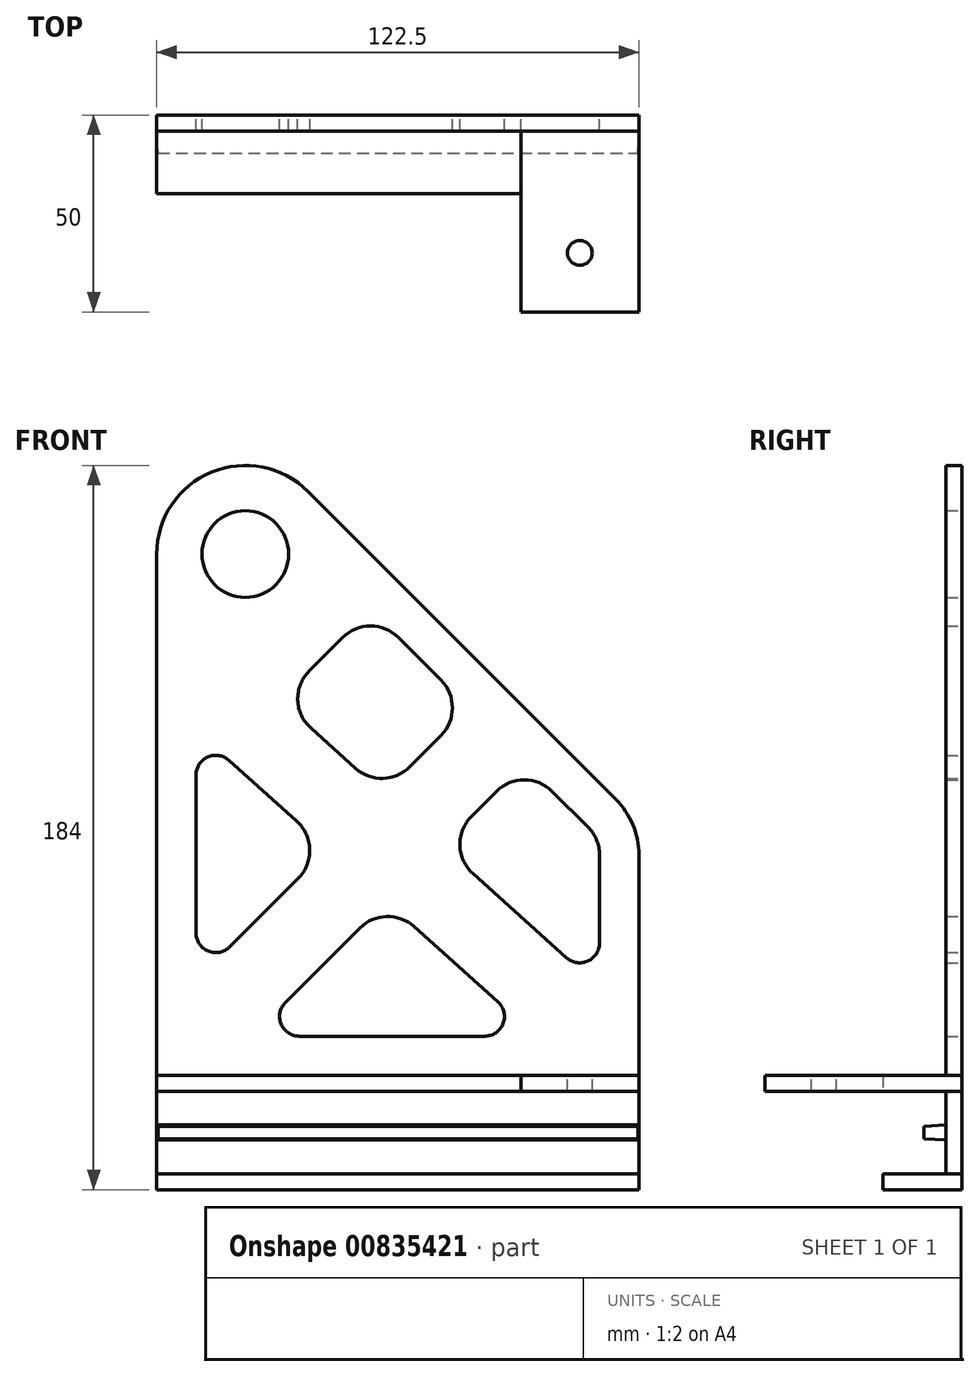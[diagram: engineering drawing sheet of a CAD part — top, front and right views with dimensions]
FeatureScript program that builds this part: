
annotation { "Feature Type Name" : "Feature", "Feature Type Description" : "" }
export const myFeature = defineFeature(function(context is Context, id is Id, definition is map)
    precondition{}
    {
        {
            var Q0;
            Q0=qCreatedBy(makeId("Front.planeOp"),FACE);
            var sketch = newSketch(context, id + "F0", { "sketchPlane" : qUnion([Q0])});
            skLineSegment(sketch, "E0.bottom", {"start": v(0, 0) * mm, "end": v(122.5, 0) * mm});
            skLineSegment(sketch, "E0.top", {"start": v(0, -4) * mm, "end": v(122.5, -4) * mm});
            skLineSegment(sketch, "E0.left", {"start": v(0, 0) * mm, "end": v(0, -4) * mm});
            skLineSegment(sketch, "E0.right", {"start": v(122.5, 0) * mm, "end": v(122.5, -4) * mm});
            skLineSegment(sketch, "E1.top", {"start": v(0, -25) * mm, "end": v(122.5, -25) * mm});
            skLineSegment(sketch, "E1.left", {"start": v(0, -4) * mm, "end": v(0, -25) * mm});
            skLineSegment(sketch, "E1.right", {"start": v(122.5, -4) * mm, "end": v(122.5, -25) * mm});
            skLineSegment(sketch, "E2", {"start": v(0, 110) * mm, "end": v(0, 132.5) * mm});
            skLineSegment(sketch, "E3", {"start": v(0, 132.5) * mm, "end": v(22.5, 132.5) * mm});
            skCircle(sketch, "E4", {"center": v(22.5, 132.5) * mm, "radius": 3.98 * mm});
            skCircle(sketch, "E5", {"center": v(22.5, 132.5) * mm, "radius": 11 * mm});
            skArc(sketch, "E6", {"start": v(38.4, 148.4) * mm, "mid": v(13.89, 153.29) * mm, "end": v(0, 132.5) * mm});
            skLineSegment(sketch, "E7", {"start": v(38.4, 148.4) * mm, "end": v(54.32, 132.5) * mm});
            skLineSegment(sketch, "E8", {"start": v(122.5, 0) * mm, "end": v(122.5, 56.04) * mm});
            skLineSegment(sketch, "E9", {"start": v(122.5, -25) * mm, "end": v(122.5, -29) * mm});
            skLineSegment(sketch, "E10", {"start": v(0, -12.6) * mm, "end": v(122.5, -12.6) * mm});
            skLineSegment(sketch, "E11", {"start": v(0, -16.4) * mm, "end": v(122.5, -16.4) * mm});
            skLineSegment(sketch, "E12", {"start": v(92.5, 0) * mm, "end": v(92.5, -4) * mm});
            skPoint(sketch, "E13.visualSharp", {"position": v(122.5, 64.32) * mm});
            skArc(sketch, "E13.filletArc", {"start": v(122.5, 56.04) * mm, "mid": v(120.98, 63.69) * mm, "end": v(116.64, 70.18) * mm});
            skPoint(sketch, "E14", {"position": v(57.96, 57.96) * mm});
            skLineSegment(sketch, "E15.trimOffspring", {"start": v(93.4, 93.4) * mm, "end": v(116.64, 70.18) * mm});
            skLineSegment(sketch, "E16", {"start": v(54.32, 132.5) * mm, "end": v(93.4, 93.4) * mm});
            skLineSegment(sketch, "E17", {"start": v(0, 110) * mm, "end": v(0, 0) * mm});
            skLineSegment(sketch, "E18.0", {"start": v(64.29, 78.43) * mm, "end": v(72.2, 86.34) * mm});
            skLineSegment(sketch, "E18.1", {"start": v(39.15, 88.29) * mm, "end": v(50.54, 78.06) * mm});
            skLineSegment(sketch, "E18.2", {"start": v(61.4, 111.29) * mm, "end": v(72.2, 100.48) * mm});
            skLineSegment(sketch, "E18.3", {"start": v(47.25, 111.29) * mm, "end": v(38.76, 102.8) * mm});
            skLineSegment(sketch, "E19.0", {"start": v(35.96, 50.1) * mm, "end": v(18.54, 32.68) * mm});
            skLineSegment(sketch, "E19.1", {"start": v(18.34, 80.1) * mm, "end": v(35.57, 64.62) * mm});
            skLineSegment(sketch, "E19.2", {"start": v(10, 76.37) * mm, "end": v(10, 36.21) * mm});
            skLineSegment(sketch, "E20.0", {"start": v(112.5, 33.63) * mm, "end": v(112.5, 56.04) * mm});
            skLineSegment(sketch, "E20.1", {"start": v(80.34, 51.3) * mm, "end": v(104.16, 29.9) * mm});
            skArc(sketch, "E20.2", {"start": v(112.5, 56.04) * mm, "mid": v(111.74, 59.86) * mm, "end": v(109.57, 63.1) * mm});
            skLineSegment(sketch, "E20.3", {"start": v(100.48, 72.2) * mm, "end": v(109.57, 63.1) * mm});
            skLineSegment(sketch, "E20.4", {"start": v(79.95, 65.8) * mm, "end": v(86.34, 72.2) * mm});
            skLineSegment(sketch, "E21.0", {"start": v(65.38, 37.85) * mm, "end": v(86.69, 18.72) * mm});
            skLineSegment(sketch, "E21.1", {"start": v(51.63, 37.48) * mm, "end": v(32.68, 18.54) * mm});
            skLineSegment(sketch, "E21.2", {"start": v(36.21, 10) * mm, "end": v(83.34, 10) * mm});
            skPoint(sketch, "E22.visualSharp", {"position": v(58.33, 44.18) * mm});
            skArc(sketch, "E22.filletArc", {"start": v(65.38, 37.85) * mm, "mid": v(58.43, 40.4) * mm, "end": v(51.63, 37.48) * mm});
            skPoint(sketch, "E23.visualSharp", {"position": v(24.14, 10) * mm});
            skArc(sketch, "E23.filletArc", {"start": v(32.68, 18.54) * mm, "mid": v(31.6, 13.09) * mm, "end": v(36.21, 10) * mm});
            skPoint(sketch, "E24.visualSharp", {"position": v(96.4, 10) * mm});
            skArc(sketch, "E24.filletArc", {"start": v(83.34, 10) * mm, "mid": v(88.01, 13.21) * mm, "end": v(86.69, 18.72) * mm});
            skPoint(sketch, "E25.visualSharp", {"position": v(112.5, 22.42) * mm});
            skArc(sketch, "E25.filletArc", {"start": v(104.16, 29.9) * mm, "mid": v(109.54, 29.06) * mm, "end": v(112.5, 33.63) * mm});
            skPoint(sketch, "E26.visualSharp", {"position": v(72.49, 58.35) * mm});
            skArc(sketch, "E26.filletArc", {"start": v(79.95, 65.8) * mm, "mid": v(77.03, 58.47) * mm, "end": v(80.34, 51.3) * mm});
            skPoint(sketch, "E27.visualSharp", {"position": v(57.59, 71.73) * mm});
            skArc(sketch, "E27.filletArc", {"start": v(50.54, 78.06) * mm, "mid": v(57.49, 75.5) * mm, "end": v(64.29, 78.43) * mm});
            skPoint(sketch, "E28.visualSharp", {"position": v(43.42, 57.57) * mm});
            skArc(sketch, "E28.filletArc", {"start": v(35.96, 50.1) * mm, "mid": v(38.89, 57.44) * mm, "end": v(35.57, 64.62) * mm});
            skPoint(sketch, "E29.visualSharp", {"position": v(93.4, 79.27) * mm});
            skArc(sketch, "E29.filletArc", {"start": v(100.48, 72.2) * mm, "mid": v(93.4, 75.13) * mm, "end": v(86.34, 72.2) * mm});
            skPoint(sketch, "E30.visualSharp", {"position": v(79.27, 93.4) * mm});
            skArc(sketch, "E30.filletArc", {"start": v(72.2, 86.34) * mm, "mid": v(75.13, 93.4) * mm, "end": v(72.2, 100.48) * mm});
            skPoint(sketch, "E31.visualSharp", {"position": v(10, 24.14) * mm});
            skArc(sketch, "E31.filletArc", {"start": v(10, 36.21) * mm, "mid": v(13.09, 31.6) * mm, "end": v(18.54, 32.68) * mm});
            skPoint(sketch, "E32.visualSharp", {"position": v(10, 87.58) * mm});
            skArc(sketch, "E32.filletArc", {"start": v(18.34, 80.1) * mm, "mid": v(12.96, 80.94) * mm, "end": v(10, 76.37) * mm});
            skPoint(sketch, "E33.visualSharp", {"position": v(54.32, 118.36) * mm});
            skArc(sketch, "E33.filletArc", {"start": v(61.4, 111.29) * mm, "mid": v(54.32, 114.22) * mm, "end": v(47.25, 111.29) * mm});
            skPoint(sketch, "E34.start.orphan", {"position": v(22.5, 110) * mm});
            skPoint(sketch, "E35.visualSharp", {"position": v(31.3, 95.34) * mm});
            skArc(sketch, "E35.filletArc", {"start": v(38.76, 102.8) * mm, "mid": v(35.83, 95.46) * mm, "end": v(39.15, 88.29) * mm});
            skLineSegment(sketch, "E36", {"start": v(0, -29) * mm, "end": v(0, -25) * mm});
            skLineSegment(sketch, "E37", {"start": v(122.5, -29) * mm, "end": v(0, -29) * mm});
            skSolve(sketch);
        }
        {
            var Q0;
            {var subQ0=sQuery(id+"F0.wireOp",EDGE,"E2");Q0=makeQuery(id+"F0.imprint","IMPRINT",FACE,{"disambiguationData":[TD([[makeQuery(id+"F0.imprint","IMPRINT",EDGE,{"derivedFrom":subQ0}),-1.0]])]});}
            var Q1;
            {var subQ3=sQuery(id+"F0.wireOp",EDGE,"E10");Q1=makeQuery(id+"F0.imprint","IMPRINT",FACE,{"disambiguationData":[TD([[makeQuery(id+"F0.imprint","IMPRINT",EDGE,{"derivedFrom":subQ3}),1.0]])]});}
            var Q2;
            {var subQ3=sQuery(id+"F0.wireOp",EDGE,"E11");Q2=makeQuery(id+"F0.imprint","IMPRINT",FACE,{"disambiguationData":[TD([[makeQuery(id+"F0.imprint","IMPRINT",EDGE,{"derivedFrom":subQ3}),-1.0]])]});}
            extrude(context, id + "F1", {"entities" : qUnion([Q0, Q1, Q2]), "depth" : 4 * mm, "offsetDistance" : 25 * mm});
        }
        {
            var Q0;
            {var subQ0=sQuery(id+"F0.wireOp",EDGE,"E0.left");Q0=makeQuery(id+"F0.imprint","IMPRINT",FACE,{"disambiguationData":[TD([[makeQuery(id+"F0.imprint","IMPRINT",EDGE,{"derivedFrom":subQ0}),1.0]])]});}
            var Q1;
            Q1=makeQuery(id+"F0.imprint","IMPRINT",FACE,{"disambiguationData":[TD([[makeQuery(id+"F0.imprint","IMPRINT",EDGE,{"derivedFrom":sQuery(id+"F0.wireOp",EDGE,"E1.top")}),-1.0]])]});
            extrude(context, id + "F2", {"entities" : qUnion([Q0, Q1]), "depth" : 20 * mm, "offsetDistance" : 25 * mm});
        }
        {
            var Q0;
            {var subQ0=sQuery(id+"F0.wireOp",EDGE,"E0.right");Q0=makeQuery(id+"F0.imprint","IMPRINT",FACE,{"disambiguationData":[TD([[makeQuery(id+"F0.imprint","IMPRINT",EDGE,{"derivedFrom":subQ0}),-1.0]])]});}
            extrude(context, id + "F3", {"entities" : qUnion([Q0]), "depth" : 50 * mm, "offsetDistance" : 25 * mm});
        }
        {
            var Q0;
            {var subQ0=sQuery(id+"F0.wireOp",EDGE,"E10");Q0=makeQuery(id+"F0.imprint","IMPRINT",FACE,{"disambiguationData":[TD([[makeQuery(id+"F0.imprint","IMPRINT",EDGE,{"derivedFrom":subQ0}),-1.0]])]});}
            extrude(context, id + "F4", {"entities" : qUnion([Q0]), "depth" : 4 * mm, "offsetDistance" : 25 * mm});
        }
        {
            var Q0;
            Q0=makeQuery(id+"F3.opExtrude","SWEPT_FACE",FACE,{"disambiguationData":[OSD([sQuery(id+"F0.wireOp",EDGE,"E0.bottom")])]});
            var sketch = newSketch(context, id + "F5", { "sketchPlane" : qUnion([Q0])});
            skCircle(sketch, "E38", {"center": v(107.5, -35) * mm, "radius": 3.15 * mm});
            skSolve(sketch);
        }
        {
            var Q0;
            Q0=makeQuery(id+"F5.imprint","IMPRINT",FACE,{"disambiguationData":[TD([[makeQuery(id+"F5.imprint","IMPRINT",EDGE,{"derivedFrom":sQuery(id+"F5.wireOp",EDGE,"E38")}),1.0]])]});
            extrude(context, id + "F6", {"entities" : qUnion([Q0]), "operationType" : NewBodyOperationType.REMOVE, "oppositeDirection" : true, "depth" : 40 * mm, "offsetDistance" : 25 * mm});
        }
        {
            var Q0;
            Q0=makeQuery(id+"F4.opExtrude","CAP_FACE",FACE,{"disambiguationData":[OSD([sQuery(id+"F0.wireOp",EDGE,"E1.left"),sQuery(id+"F0.wireOp",EDGE,"E1.right"),sQuery(id+"F0.wireOp",EDGE,"E10"),sQuery(id+"F0.wireOp",EDGE,"E11")])],"isStart":false});
            extrude(context, id + "F7", {"entities" : qUnion([Q0]), "operationType" : NewBodyOperationType.ADD, "depth" : 5.6 * mm, "offsetDistance" : 25 * mm, "hasDraft" : true, "draftAngle" : 3 * degree, "draftPullDirection" : true});
        }
    });
